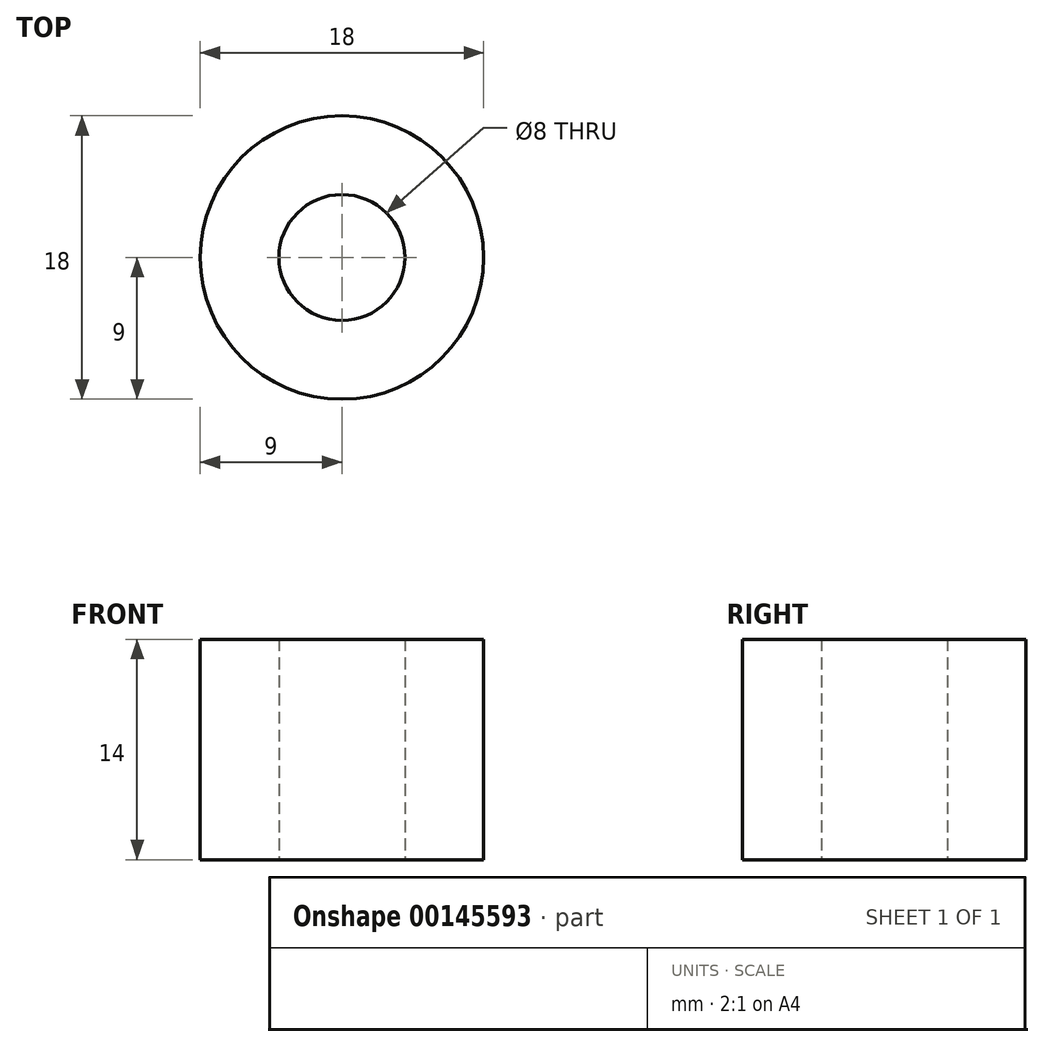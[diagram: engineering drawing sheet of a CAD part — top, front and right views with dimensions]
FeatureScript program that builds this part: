
annotation { "Feature Type Name" : "Feature", "Feature Type Description" : "" }
export const myFeature = defineFeature(function(context is Context, id is Id, definition is map)
    precondition{}
    {
        {
            var Q0;
            Q0=qCreatedBy(makeId("Top.planeOp"),FACE);
            var sketch = newSketch(context, id + "F0", { "sketchPlane" : qUnion([Q0])});
            skLineSegment(sketch, "E0.bottom", {"start": v(0, 0) * mm, "end": v(52, 0) * mm});
            skLineSegment(sketch, "E0.top", {"start": v(0, 22) * mm, "end": v(52, 22) * mm});
            skLineSegment(sketch, "E0.left", {"start": v(0, 0) * mm, "end": v(0, 22) * mm});
            skLineSegment(sketch, "E0.right", {"start": v(52, 0) * mm, "end": v(52, 22) * mm});
            skCircle(sketch, "E1", {"center": v(52, -18) * mm, "radius": 4 * mm});
            skCircle(sketch, "E2", {"center": v(52, -18) * mm, "radius": 9 * mm});
            skLineSegment(sketch, "E3.bottom", {"start": v(52, 0) * mm, "end": v(47, 0) * mm});
            skLineSegment(sketch, "E3.right", {"start": v(47, 0) * mm, "end": v(47, -10.52) * mm});
            skPoint(sketch, "E4", {"position": v(52, 11) * mm});
            skPoint(sketch, "E5", {"position": v(0, 11) * mm});
            skLineSegment(sketch, "E6", {"start": v(0, 11) * mm, "end": v(52, 11) * mm, "construction": true});
            skLineSegment(sketch, "E7", {"start": v(52, 0) * mm, "end": v(52, -18) * mm});
            skSolve(sketch);
        }
        {
            var Q0;
            {var subQ1=sQuery(id+"F0.wireOp",EDGE,"E0.top");Q0=makeQuery(id+"F0.imprint","IMPRINT",FACE,{"disambiguationData":[TD([[makeQuery(id+"F0.imprint","IMPRINT",EDGE,{"derivedFrom":subQ1}),-1.0]])]});}
            var Q1;
            {var subQ5=sQuery(id+"F0.wireOp",EDGE,"E2");var subQ6=sQuery(id+"F0.wireOp",EDGE,"E0.bottom");var subQ7=makeQuery(id+"F0.imprint","INTERSECT",VERTEX,{"derivedFrom":[subQ6,subQ5]});Q1=makeQuery(id+"F0.imprint","IMPRINT",FACE,{"disambiguationData":[TD([[makeQuery(id+"F0.imprint","IMPRINT",EDGE,{"disambiguationData":[TD([[subQ7,1.0]])],"derivedFrom":subQ6}),1.0]])]});}
            extrude(context, id + "F1", {"entities" : qUnion([Q0, Q1]), "depth" : 52.6 * mm});
        }
        {
            var Q0;
            {var subQ5=sQuery(id+"F0.wireOp",EDGE,"E3.bottom");Q0=makeQuery(id+"F0.imprint","IMPRINT",FACE,{"disambiguationData":[TD([[makeQuery(id+"F0.imprint","IMPRINT",EDGE,{"derivedFrom":subQ5}),1.0]])]});}
            var Q1;
            {var subQ2=sQuery(id+"F0.wireOp",EDGE,"E2");var subQ7=makeQuery(id+"F0.imprint","INTERSECT",VERTEX,{"derivedFrom":[subQ2,sQuery(id+"F0.wireOp",EDGE,"E3.right")]});Q1=makeQuery(id+"F0.imprint","IMPRINT",FACE,{"disambiguationData":[TD([[makeQuery(id+"F0.imprint","IMPRINT",EDGE,{"disambiguationData":[TD([[subQ7,1.0]])],"derivedFrom":subQ2}),1.0]])]});}
            var Q2;
            {var subQ1=sQuery(id+"F0.wireOp",EDGE,"E1");Q2=makeQuery(id+"F0.imprint","IMPRINT",FACE,{"disambiguationData":[TD([[makeQuery(id+"F0.imprint","IMPRINT",EDGE,{"derivedFrom":subQ1}),-1.0]])]});}
            extrude(context, id + "F2", {"entities" : qUnion([Q0, Q1, Q2]), "operationType" : NewBodyOperationType.ADD, "depth" : 14 * mm, "offsetDistance" : 25 * mm});
        }
        {
            var Q0;
            Q0=makeQuery(id+"F1.opExtrude","SWEPT_FACE",FACE,{"disambiguationData":[OSD([sQuery(id+"F0.wireOp",EDGE,"E0.left")])]});
            var sketch = newSketch(context, id + "F3", { "sketchPlane" : qUnion([Q0])});
            skCircle(sketch, "E8", {"center": v(-11, 9) * mm, "radius": 7.5 * mm});
            skLineSegment(sketch, "E9", {"start": v(-22, 47.6) * mm, "end": v(0, 47.6) * mm, "construction": true});
            skLineSegment(sketch, "E10", {"start": v(-22, 9) * mm, "end": v(0, 9) * mm, "construction": true});
            skLineSegment(sketch, "E11", {"start": v(-11, 9) * mm, "end": v(-11, 0) * mm, "construction": true});
            skLineSegment(sketch, "E12", {"start": v(-11, 0) * mm, "end": v(-11.5, 0) * mm});
            skLineSegment(sketch, "E13", {"start": v(-11.5, 0) * mm, "end": v(-11.5, 1.52) * mm});
            skLineSegment(sketch, "E14", {"start": v(-11.5, 1.52) * mm, "end": v(-10.5, 1.52) * mm});
            skLineSegment(sketch, "E15", {"start": v(-10.5, 1.52) * mm, "end": v(-10.5, 0) * mm});
            skLineSegment(sketch, "E16", {"start": v(-10.5, 0) * mm, "end": v(-11, 0) * mm});
            skCircle(sketch, "E17", {"center": v(-11, 47.6) * mm, "radius": 7.45 * mm});
            skLineSegment(sketch, "E18", {"start": v(-11, 47.6) * mm, "end": v(-11, 9) * mm, "construction": true});
            skLineSegment(sketch, "E19", {"start": v(-11, 19.6) * mm, "end": v(-16.3, 14.3) * mm, "construction": true});
            skLineSegment(sketch, "E20", {"start": v(-16.3, 14.3) * mm, "end": v(-11, 19.6) * mm});
            skLineSegment(sketch, "E21", {"start": v(-5.7, 14.3) * mm, "end": v(-11, 19.6) * mm});
            skLineSegment(sketch, "E22", {"start": v(-18.41, 17) * mm, "end": v(-3.44, 17) * mm});
            skSolve(sketch);
        }
        {
            var Q0;
            {var subQ0=sQuery(id+"F3.wireOp",EDGE,"E14");Q0=makeQuery(id+"F3.imprint","IMPRINT",FACE,{"disambiguationData":[TD([[makeQuery(id+"F3.imprint","IMPRINT",EDGE,{"derivedFrom":subQ0}),1.0]])]});}
            var Q1;
            {var subQ0=sQuery(id+"F3.wireOp",EDGE,"E20");var subQ1=sQuery(id+"F3.wireOp",EDGE,"E8");var subQ2=makeQuery(id+"F3.imprint","INTERSECT",VERTEX,{"derivedFrom":[subQ1,subQ0]});Q1=makeQuery(id+"F3.imprint","IMPRINT",FACE,{"disambiguationData":[TD([[makeQuery(id+"F3.imprint","IMPRINT",EDGE,{"disambiguationData":[TD([[subQ2,1.0]])],"derivedFrom":subQ1}),-1.0]])]});}
            var Q2;
            {var subQ0=sQuery(id+"F3.wireOp",EDGE,"E21");var subQ1=sQuery(id+"F3.wireOp",EDGE,"E8");var subQ2=makeQuery(id+"F3.imprint","INTERSECT",VERTEX,{"derivedFrom":[subQ1,subQ0]});Q2=makeQuery(id+"F3.imprint","IMPRINT",FACE,{"disambiguationData":[TD([[makeQuery(id+"F3.imprint","IMPRINT",EDGE,{"disambiguationData":[TD([[subQ2,-1.0]])],"derivedFrom":subQ1}),-1.0]])]});}
            var Q3;
            {var subQ0=sQuery(id+"F3.wireOp",EDGE,"035e7980-5c30-4cae-b493-835d1dc4b1b4");var subQ1=makeQuery(id+"F1.opExtrude","CAP_EDGE",EDGE,{"disambiguationData":[OSD([sQuery(id+"F0.wireOp",EDGE,"E0.left")])],"isStart":false});var subQ2=makeQuery(id+"F3.imprint","INTERSECT",VERTEX,{"disambiguationData":[OD(0.0)],"derivedFrom":[subQ1,subQ0]});Q3=makeQuery(id+"F3.imprint","IMPRINT",FACE,{"disambiguationData":[TD([[makeQuery(id+"F3.imprint","IMPRINT",EDGE,{"disambiguationData":[TD([[subQ2,1.0]])],"derivedFrom":subQ0}),-1.0]])]});}
            var Q4;
            {var subQ0=sQuery(id+"F3.wireOp",EDGE,"035e7980-5c30-4cae-b493-835d1dc4b1b4");var subQ1=makeQuery(id+"F1.opExtrude","CAP_EDGE",EDGE,{"disambiguationData":[OSD([sQuery(id+"F0.wireOp",EDGE,"E0.left")])],"isStart":false});var subQ2=makeQuery(id+"F3.imprint","INTERSECT",VERTEX,{"disambiguationData":[OD(0.0)],"derivedFrom":[subQ1,subQ0]});Q4=makeQuery(id+"F3.imprint","IMPRINT",FACE,{"disambiguationData":[TD([[makeQuery(id+"F3.imprint","IMPRINT",EDGE,{"disambiguationData":[TD([[subQ2,1.0]])],"derivedFrom":subQ0}),1.0]])]});}
            var Q5;
            Q5=makeQuery(id+"F3.imprint","IMPRINT",FACE,{"disambiguationData":[TD([[makeQuery(id+"F3.imprint","IMPRINT",EDGE,{"derivedFrom":sQuery(id+"F3.wireOp",EDGE,"E12")}),-1.0]])]});
            var Q6;
            {var subQ0=sQuery(id+"F3.wireOp",EDGE,"E17");var subQ1=makeQuery(id+"F1.opExtrude","CAP_EDGE",EDGE,{"disambiguationData":[OSD([sQuery(id+"F0.wireOp",EDGE,"E0.left")])],"isStart":false});var subQ2=makeQuery(id+"F3.imprint","INTERSECT",VERTEX,{"disambiguationData":[OD(0.0)],"derivedFrom":[subQ1,subQ0]});Q6=makeQuery(id+"F3.imprint","IMPRINT",FACE,{"disambiguationData":[TD([[makeQuery(id+"F3.imprint","IMPRINT",EDGE,{"disambiguationData":[TD([[subQ2,1.0]])],"derivedFrom":subQ0}),1.0]])]});}
            extrude(context, id + "F4", {"entities" : qUnion([Q0, Q1, Q2, Q3, Q4, Q5, Q6]), "operationType" : NewBodyOperationType.REMOVE, "endBound" : BoundingType.THROUGH_ALL, "oppositeDirection" : true, "depth" : 25 * mm, "offsetDistance" : 25 * mm});
        }
        {
            var Q0;
            Q0=makeQuery(id+"F1.opExtrude","SWEPT_FACE",FACE,{"disambiguationData":[OSD([sQuery(id+"F0.wireOp",EDGE,"E0.bottom")])]});
            var sketch = newSketch(context, id + "F5", { "sketchPlane" : qUnion([Q0])});
            skLineSegment(sketch, "E23.bottom", {"start": v(0, 29.9) * mm, "end": v(10, 29.9) * mm});
            skLineSegment(sketch, "E23.top", {"start": v(0, 9.9) * mm, "end": v(10, 9.9) * mm});
            skLineSegment(sketch, "E23.left", {"start": v(0, 29.9) * mm, "end": v(0, 9.9) * mm});
            skLineSegment(sketch, "E23.right", {"start": v(10, 29.9) * mm, "end": v(10, 9.9) * mm});
            skLineSegment(sketch, "E24.bottom", {"start": v(52, 41.1) * mm, "end": v(42, 41.1) * mm});
            skLineSegment(sketch, "E24.top", {"start": v(52, 21.1) * mm, "end": v(42, 21.1) * mm});
            skLineSegment(sketch, "E24.left", {"start": v(52, 41.1) * mm, "end": v(52, 21.1) * mm});
            skLineSegment(sketch, "E24.right", {"start": v(42, 41.1) * mm, "end": v(42, 21.1) * mm});
            skPoint(sketch, "E25", {"position": v(0, 9.4) * mm});
            skPoint(sketch, "E26", {"position": v(26, 52.6) * mm});
            skLineSegment(sketch, "E27", {"start": v(26, 52.6) * mm, "end": v(26, 0) * mm, "construction": true});
            skLineSegment(sketch, "E28.bottom", {"start": v(21, 52.6) * mm, "end": v(31, 52.6) * mm});
            skLineSegment(sketch, "E28.top", {"start": v(21, 37.6) * mm, "end": v(31, 37.6) * mm});
            skLineSegment(sketch, "E28.left", {"start": v(21, 52.6) * mm, "end": v(21, 37.6) * mm});
            skLineSegment(sketch, "E28.right", {"start": v(31, 52.6) * mm, "end": v(31, 37.6) * mm});
            skLineSegment(sketch, "E29", {"start": v(7, 52.6) * mm, "end": v(7, 29.9) * mm, "construction": true});
            skCircle(sketch, "E30", {"center": v(7, 44.9) * mm, "radius": 0.8 * mm});
            skCircle(sketch, "E31", {"center": v(7, 34.9) * mm, "radius": 0.8 * mm});
            skSolve(sketch);
        }
        {
            var Q0;
            Q0=makeQuery(id+"F5.imprint","IMPRINT",FACE,{"disambiguationData":[TD([[makeQuery(id+"F5.imprint","IMPRINT",EDGE,{"derivedFrom":sQuery(id+"F5.wireOp",EDGE,"E31")}),1.0]])]});
            extrude(context, id + "F6", {"entities" : qUnion([Q0]), "operationType" : NewBodyOperationType.REMOVE, "oppositeDirection" : true, "depth" : 7 * mm, "offsetDistance" : 25 * mm});
        }
        {
            var Q0;
            Q0=makeQuery(id+"F5.imprint","IMPRINT",FACE,{"disambiguationData":[TD([[makeQuery(id+"F5.imprint","IMPRINT",EDGE,{"derivedFrom":sQuery(id+"F5.wireOp",EDGE,"E30")}),1.0]])]});
            var Q1;
            Q1=sQuery(id+"F5.wireOp",EDGE,"E30");
            extrude(context, id + "F7", {"entities" : qUnion([Q0]), "operationType" : NewBodyOperationType.REMOVE, "surfaceEntities" : qUnion([Q1]), "oppositeDirection" : true, "depth" : 3 * mm, "offsetDistance" : 25 * mm});
        }
        {
            var Q0;
            Q0=makeQuery(id+"F5.imprint","IMPRINT",FACE,{"disambiguationData":[TD([[makeQuery(id+"F5.imprint","IMPRINT",EDGE,{"derivedFrom":sQuery(id+"F5.wireOp",EDGE,"E23.bottom")}),-1.0]])]});
            var Q1;
            Q1=makeQuery(id+"F5.imprint","IMPRINT",FACE,{"disambiguationData":[TD([[makeQuery(id+"F5.imprint","IMPRINT",EDGE,{"derivedFrom":sQuery(id+"F5.wireOp",EDGE,"E24.bottom")}),1.0]])]});
            extrude(context, id + "F8", {"entities" : qUnion([Q0, Q1]), "operationType" : NewBodyOperationType.ADD, "depth" : 7 * mm, "offsetDistance" : 25 * mm});
        }
        {
            var Q0;
            Q0=makeQuery(id+"F8.opExtrude","CAP_EDGE",EDGE,{"disambiguationData":[OSD([sQuery(id+"F5.wireOp",EDGE,"E23.top")])],"isStart":false});
            var Q1;
            Q1=makeQuery(id+"F8.opExtrude","CAP_EDGE",EDGE,{"disambiguationData":[OSD([sQuery(id+"F5.wireOp",EDGE,"E24.top")])],"isStart":false});
            chamfer(context, id + "F9", {"entities" : qUnion([Q0, Q1]), "width" : 10 * mm, "tangentPropagation" : true});
        }
        {
            var Q0;
            Q0=makeQuery(id+"F8.opExtrude","SWEPT_FACE",FACE,{"disambiguationData":[OSD([sQuery(id+"F5.wireOp",EDGE,"E23.bottom")])]});
            var sketch = newSketch(context, id + "F10", { "sketchPlane" : qUnion([Q0])});
            skLineSegment(sketch, "E32", {"start": v(-935.9, 0) * mm, "end": v(-935.88, -4.54) * mm});
            skLineSegment(sketch, "E33.left", {"start": v(0, -3.25) * mm, "end": v(0, -1.6) * mm});
            skLineSegment(sketch, "E34", {"start": v(6, -2.5) * mm, "end": v(7, -2.5) * mm});
            skLineSegment(sketch, "E35", {"start": v(4, -2.5) * mm, "end": v(5, -2.5) * mm});
            skLineSegment(sketch, "E36", {"start": v(0, -2.5) * mm, "end": v(1, -2.5) * mm});
            skLineSegment(sketch, "E37", {"start": v(7, -1.6) * mm, "end": v(8, -1.6) * mm});
            skLineSegment(sketch, "E38", {"start": v(2, -2.5) * mm, "end": v(3, -2.5) * mm});
            skLineSegment(sketch, "E39", {"start": v(3, -1.6) * mm, "end": v(4, -1.6) * mm});
            skLineSegment(sketch, "E40", {"start": v(8, -2.5) * mm, "end": v(9, -2.5) * mm});
            skLineSegment(sketch, "E41", {"start": v(8, -1.6) * mm, "end": v(8, -2.5) * mm});
            skLineSegment(sketch, "E42", {"start": v(9, -2.5) * mm, "end": v(9, -1.6) * mm});
            skLineSegment(sketch, "E43", {"start": v(10, -1.6) * mm, "end": v(10, -2.5) * mm});
            skLineSegment(sketch, "E44", {"start": v(6, -1.6) * mm, "end": v(6, -2.5) * mm});
            skLineSegment(sketch, "E45", {"start": v(2, -1.6) * mm, "end": v(2, -2.5) * mm});
            skLineSegment(sketch, "E46", {"start": v(1, -1.6) * mm, "end": v(2, -1.6) * mm});
            skLineSegment(sketch, "E47", {"start": v(1, -2.5) * mm, "end": v(1, -1.6) * mm});
            skLineSegment(sketch, "E48", {"start": v(9, -1.6) * mm, "end": v(10, -1.6) * mm});
            skLineSegment(sketch, "E49", {"start": v(5, -1.6) * mm, "end": v(6, -1.6) * mm});
            skLineSegment(sketch, "E50", {"start": v(5, -2.5) * mm, "end": v(5, -1.6) * mm});
            skLineSegment(sketch, "E51", {"start": v(3, -2.5) * mm, "end": v(3, -1.6) * mm});
            skLineSegment(sketch, "E52", {"start": v(4, -1.6) * mm, "end": v(4, -2.5) * mm});
            skLineSegment(sketch, "E53", {"start": v(7, -2.5) * mm, "end": v(7, -1.6) * mm});
            skLineSegment(sketch, "E54", {"start": v(0, -1.6) * mm, "end": v(0, -2.5) * mm});
            skLineSegment(sketch, "E55", {"start": v(10, -2.5) * mm, "end": v(10, -3.25) * mm});
            skLineSegment(sketch, "E56", {"start": v(0, -3.25) * mm, "end": v(10, -3.25) * mm});
            skLineSegment(sketch, "E57", {"start": v(5.3, -1.6) * mm, "end": v(5.3, 0) * mm});
            skSolve(sketch);
        }
        {
            var Q0;
            Q0=qSketchRegion(id+"F10",true);
            extrude(context, id + "F11", {"entities" : qUnion([Q0]), "operationType" : NewBodyOperationType.REMOVE, "oppositeDirection" : true, "depth" : 6 * mm});
        }
        {
            var Q0;
            Q0=makeQuery(id+"F8.opExtrude","SWEPT_FACE",FACE,{"disambiguationData":[OSD([sQuery(id+"F5.wireOp",EDGE,"E24.bottom")])]});
            var sketch = newSketch(context, id + "F12", { "sketchPlane" : qUnion([Q0])});
            skLineSegment(sketch, "E58.left", {"start": v(42, -3.25) * mm, "end": v(42, -1.6) * mm});
            skLineSegment(sketch, "E59", {"start": v(48, -2.5) * mm, "end": v(49, -2.5) * mm});
            skLineSegment(sketch, "E60", {"start": v(46, -2.5) * mm, "end": v(47, -2.5) * mm});
            skLineSegment(sketch, "E61", {"start": v(42, -2.5) * mm, "end": v(43, -2.5) * mm});
            skLineSegment(sketch, "E62", {"start": v(49, -1.6) * mm, "end": v(50, -1.6) * mm});
            skLineSegment(sketch, "E63", {"start": v(44, -2.5) * mm, "end": v(45, -2.5) * mm});
            skLineSegment(sketch, "E64", {"start": v(45, -1.6) * mm, "end": v(46, -1.6) * mm});
            skLineSegment(sketch, "E65", {"start": v(50, -2.5) * mm, "end": v(51, -2.5) * mm});
            skLineSegment(sketch, "E66", {"start": v(50, -1.6) * mm, "end": v(50, -2.5) * mm});
            skLineSegment(sketch, "E67", {"start": v(51, -2.5) * mm, "end": v(51, -1.6) * mm});
            skLineSegment(sketch, "E68", {"start": v(52, -1.6) * mm, "end": v(52, -2.5) * mm});
            skLineSegment(sketch, "E69", {"start": v(48, -1.6) * mm, "end": v(48, -2.5) * mm});
            skLineSegment(sketch, "E70", {"start": v(44, -1.6) * mm, "end": v(44, -2.5) * mm});
            skLineSegment(sketch, "E71", {"start": v(43, -1.6) * mm, "end": v(44, -1.6) * mm});
            skLineSegment(sketch, "E72", {"start": v(43, -2.5) * mm, "end": v(43, -1.6) * mm});
            skLineSegment(sketch, "E73", {"start": v(51, -1.6) * mm, "end": v(52, -1.6) * mm});
            skLineSegment(sketch, "E74", {"start": v(47, -1.6) * mm, "end": v(48, -1.6) * mm});
            skLineSegment(sketch, "E75", {"start": v(47, -2.5) * mm, "end": v(47, -1.6) * mm});
            skLineSegment(sketch, "E76", {"start": v(45, -2.5) * mm, "end": v(45, -1.6) * mm});
            skLineSegment(sketch, "E77", {"start": v(46, -1.6) * mm, "end": v(46, -2.5) * mm});
            skLineSegment(sketch, "E78", {"start": v(49, -2.5) * mm, "end": v(49, -1.6) * mm});
            skLineSegment(sketch, "E79", {"start": v(42, -1.6) * mm, "end": v(42, -2.5) * mm});
            skLineSegment(sketch, "E80", {"start": v(52, -2.5) * mm, "end": v(52, -3.25) * mm});
            skLineSegment(sketch, "E81", {"start": v(42, -3.25) * mm, "end": v(52, -3.25) * mm});
            skLineSegment(sketch, "E82", {"start": v(47.23, -1.6) * mm, "end": v(47.23, 0) * mm});
            skSolve(sketch);
        }
        {
            var Q0;
            Q0=qSketchRegion(id+"F12",true);
            extrude(context, id + "F13", {"entities" : qUnion([Q0]), "operationType" : NewBodyOperationType.REMOVE, "oppositeDirection" : true, "depth" : 6 * mm});
        }
        {
            var Q0;
            Q0=makeQuery(id+"F1.opExtrude","SWEPT_FACE",FACE,{"disambiguationData":[OSD([sQuery(id+"F0.wireOp",EDGE,"E0.top")])]});
            var sketch = newSketch(context, id + "F14", { "sketchPlane" : qUnion([Q0])});
            skLineSegment(sketch, "E83.bottom", {"start": v(-52, 9.9) * mm, "end": v(-42, 9.9) * mm});
            skLineSegment(sketch, "E83.top", {"start": v(-52, 29.9) * mm, "end": v(-42, 29.9) * mm});
            skLineSegment(sketch, "E83.left", {"start": v(-52, 9.9) * mm, "end": v(-52, 29.9) * mm});
            skLineSegment(sketch, "E83.right", {"start": v(-42, 9.9) * mm, "end": v(-42, 29.9) * mm});
            skLineSegment(sketch, "E84.bottom", {"start": v(0, 41.1) * mm, "end": v(-10, 41.1) * mm});
            skLineSegment(sketch, "E84.top", {"start": v(0, 21.1) * mm, "end": v(-10, 21.1) * mm});
            skLineSegment(sketch, "E84.left", {"start": v(0, 41.1) * mm, "end": v(0, 21.1) * mm});
            skLineSegment(sketch, "E84.right", {"start": v(-10, 41.1) * mm, "end": v(-10, 21.1) * mm});
            skSolve(sketch);
        }
        {
            var Q0;
            Q0=qSketchRegion(id+"F14",true);
            extrude(context, id + "F15", {"entities" : qUnion([Q0]), "operationType" : NewBodyOperationType.ADD, "depth" : 7 * mm});
        }
        {
            var Q0;
            Q0=makeQuery(id+"F15.opExtrude","CAP_EDGE",EDGE,{"disambiguationData":[OSD([sQuery(id+"F14.wireOp",EDGE,"E84.top")])],"isStart":false});
            var Q1;
            Q1=makeQuery(id+"F15.opExtrude","CAP_EDGE",EDGE,{"disambiguationData":[OSD([sQuery(id+"F14.wireOp",EDGE,"E83.bottom")])],"isStart":false});
            chamfer(context, id + "F16", {"entities" : qUnion([Q0, Q1]), "width" : 10 * mm, "tangentPropagation" : true});
        }
        {
            var Q0;
            Q0=makeQuery(id+"F15.opExtrude","SWEPT_FACE",FACE,{"disambiguationData":[OSD([sQuery(id+"F14.wireOp",EDGE,"E83.top")])]});
            var sketch = newSketch(context, id + "F17", { "sketchPlane" : qUnion([Q0])});
            skLineSegment(sketch, "E85.left", {"start": v(42, 23.6) * mm, "end": v(42, 25.25) * mm});
            skLineSegment(sketch, "E86", {"start": v(48, 24.35) * mm, "end": v(49, 24.35) * mm});
            skLineSegment(sketch, "E87", {"start": v(46, 24.35) * mm, "end": v(47, 24.35) * mm});
            skLineSegment(sketch, "E88", {"start": v(42, 24.35) * mm, "end": v(43, 24.35) * mm});
            skLineSegment(sketch, "E89", {"start": v(49, 25.25) * mm, "end": v(50, 25.25) * mm});
            skLineSegment(sketch, "E90", {"start": v(44, 24.35) * mm, "end": v(45, 24.35) * mm});
            skLineSegment(sketch, "E91", {"start": v(45, 25.25) * mm, "end": v(46, 25.25) * mm});
            skLineSegment(sketch, "E92", {"start": v(50, 24.35) * mm, "end": v(51, 24.35) * mm});
            skLineSegment(sketch, "E93", {"start": v(50, 25.25) * mm, "end": v(50, 24.35) * mm});
            skLineSegment(sketch, "E94", {"start": v(51, 24.35) * mm, "end": v(51, 25.25) * mm});
            skLineSegment(sketch, "E95", {"start": v(52, 25.25) * mm, "end": v(52, 24.35) * mm});
            skLineSegment(sketch, "E96", {"start": v(48, 25.25) * mm, "end": v(48, 24.35) * mm});
            skLineSegment(sketch, "E97", {"start": v(44, 25.25) * mm, "end": v(44, 24.35) * mm});
            skLineSegment(sketch, "E98", {"start": v(43, 25.25) * mm, "end": v(44, 25.25) * mm});
            skLineSegment(sketch, "E99", {"start": v(43, 24.35) * mm, "end": v(43, 25.25) * mm});
            skLineSegment(sketch, "E100", {"start": v(51, 25.25) * mm, "end": v(52, 25.25) * mm});
            skLineSegment(sketch, "E101", {"start": v(47, 25.25) * mm, "end": v(48, 25.25) * mm});
            skLineSegment(sketch, "E102", {"start": v(47, 24.35) * mm, "end": v(47, 25.25) * mm});
            skLineSegment(sketch, "E103", {"start": v(45, 24.35) * mm, "end": v(45, 25.25) * mm});
            skLineSegment(sketch, "E104", {"start": v(46, 25.25) * mm, "end": v(46, 24.35) * mm});
            skLineSegment(sketch, "E105", {"start": v(49, 24.35) * mm, "end": v(49, 25.25) * mm});
            skLineSegment(sketch, "E106", {"start": v(42, 25.25) * mm, "end": v(42, 24.35) * mm});
            skLineSegment(sketch, "E107", {"start": v(52, 24.35) * mm, "end": v(52, 23.6) * mm});
            skLineSegment(sketch, "E108", {"start": v(42, 23.6) * mm, "end": v(52, 23.6) * mm});
            skLineSegment(sketch, "E109", {"start": v(47, 23.6) * mm, "end": v(47, 22) * mm});
            skSolve(sketch);
        }
        {
            var Q0;
            {var subQ4=sQuery(id+"F17.wireOp",EDGE,"E85.left");Q0=makeQuery(id+"F17.imprint","IMPRINT",FACE,{"disambiguationData":[TD([[makeQuery(id+"F17.imprint","IMPRINT",EDGE,{"derivedFrom":subQ4}),1.0]])]});}
            extrude(context, id + "F18", {"entities" : qUnion([Q0]), "operationType" : NewBodyOperationType.REMOVE, "oppositeDirection" : true, "depth" : 6 * mm});
        }
        {
            var Q0;
            Q0=makeQuery(id+"F15.opExtrude","SWEPT_FACE",FACE,{"disambiguationData":[OSD([sQuery(id+"F14.wireOp",EDGE,"E84.bottom")])]});
            var sketch = newSketch(context, id + "F19", { "sketchPlane" : qUnion([Q0])});
            skLineSegment(sketch, "E110", {"start": v(6, 24.35) * mm, "end": v(7, 24.35) * mm});
            skLineSegment(sketch, "E111", {"start": v(4, 24.35) * mm, "end": v(5, 24.35) * mm});
            skLineSegment(sketch, "E112", {"start": v(0, 24.35) * mm, "end": v(1, 24.35) * mm});
            skLineSegment(sketch, "E113", {"start": v(7, 25.25) * mm, "end": v(8, 25.25) * mm});
            skLineSegment(sketch, "E114", {"start": v(2, 24.35) * mm, "end": v(3, 24.35) * mm});
            skLineSegment(sketch, "E115", {"start": v(3, 25.25) * mm, "end": v(4, 25.25) * mm});
            skLineSegment(sketch, "E116", {"start": v(8, 24.35) * mm, "end": v(9, 24.35) * mm});
            skLineSegment(sketch, "E117", {"start": v(8, 25.25) * mm, "end": v(8, 24.35) * mm});
            skLineSegment(sketch, "E118", {"start": v(9, 24.35) * mm, "end": v(9, 25.25) * mm});
            skLineSegment(sketch, "E119", {"start": v(10, 25.25) * mm, "end": v(10, 24.35) * mm});
            skLineSegment(sketch, "E120", {"start": v(6, 25.25) * mm, "end": v(6, 24.35) * mm});
            skLineSegment(sketch, "E121", {"start": v(2, 25.25) * mm, "end": v(2, 24.35) * mm});
            skLineSegment(sketch, "E122", {"start": v(1, 25.25) * mm, "end": v(2, 25.25) * mm});
            skLineSegment(sketch, "E123", {"start": v(1, 24.35) * mm, "end": v(1, 25.25) * mm});
            skLineSegment(sketch, "E124", {"start": v(9, 25.25) * mm, "end": v(10, 25.25) * mm});
            skLineSegment(sketch, "E125", {"start": v(5, 25.25) * mm, "end": v(6, 25.25) * mm});
            skLineSegment(sketch, "E126", {"start": v(5, 24.35) * mm, "end": v(5, 25.25) * mm});
            skLineSegment(sketch, "E127", {"start": v(3, 24.35) * mm, "end": v(3, 25.25) * mm});
            skLineSegment(sketch, "E128", {"start": v(4, 25.25) * mm, "end": v(4, 24.35) * mm});
            skLineSegment(sketch, "E129", {"start": v(7, 24.35) * mm, "end": v(7, 25.25) * mm});
            skLineSegment(sketch, "E130", {"start": v(0, 23.6) * mm, "end": v(10, 23.6) * mm});
            skSolve(sketch);
        }
        {
            var Q0;
            Q0=makeQuery(id+"F19.imprint","IMPRINT",FACE,{"disambiguationData":[TD([[makeQuery(id+"F19.imprint","IMPRINT",EDGE,{"derivedFrom":sQuery(id+"F19.wireOp",EDGE,"E110")}),-1.0]])]});
            extrude(context, id + "F20", {"entities" : qUnion([Q0]), "operationType" : NewBodyOperationType.REMOVE, "oppositeDirection" : true, "depth" : 6 * mm});
        }
        {
            var Q0;
            Q0=makeQuery(id+"F1.opExtrude","SWEPT_FACE",FACE,{"disambiguationData":[OSD([sQuery(id+"F0.wireOp",EDGE,"E0.top")])]});
            var sketch = newSketch(context, id + "F21", { "sketchPlane" : qUnion([Q0])});
            skCircle(sketch, "E131", {"center": v(-26, 15) * mm, "radius": 1.3 * mm});
            skPoint(sketch, "E132", {"position": v(-26, 52.6) * mm});
            skLineSegment(sketch, "E133", {"start": v(-26, 52.6) * mm, "end": v(-26, 0) * mm, "construction": true});
            skCircle(sketch, "E134", {"center": v(-30.5, 20) * mm, "radius": 1.3 * mm});
            skCircle(sketch, "E135", {"center": v(-21.5, 20) * mm, "radius": 1.3 * mm});
            skLineSegment(sketch, "E136", {"start": v(-52, 20) * mm, "end": v(0, 20) * mm, "construction": true});
            skCircle(sketch, "E137", {"center": v(-26, 35) * mm, "radius": 1.3 * mm});
            skCircle(sketch, "E138", {"center": v(-30.5, 30) * mm, "radius": 1.3 * mm});
            skCircle(sketch, "E139", {"center": v(-21.5, 30) * mm, "radius": 1.3 * mm});
            skSolve(sketch);
        }
        {
            var Q0;
            Q0=makeQuery(id+"F21.imprint","IMPRINT",FACE,{"disambiguationData":[TD([[makeQuery(id+"F21.imprint","IMPRINT",EDGE,{"derivedFrom":sQuery(id+"F21.wireOp",EDGE,"E134")}),1.0]])]});
            var Q1;
            Q1=makeQuery(id+"F21.imprint","IMPRINT",FACE,{"disambiguationData":[TD([[makeQuery(id+"F21.imprint","IMPRINT",EDGE,{"derivedFrom":sQuery(id+"F21.wireOp",EDGE,"E135")}),1.0]])]});
            var Q2;
            Q2=makeQuery(id+"F21.imprint","IMPRINT",FACE,{"disambiguationData":[TD([[makeQuery(id+"F21.imprint","IMPRINT",EDGE,{"derivedFrom":sQuery(id+"F21.wireOp",EDGE,"E138")}),1.0]])]});
            var Q3;
            Q3=makeQuery(id+"F21.imprint","IMPRINT",FACE,{"disambiguationData":[TD([[makeQuery(id+"F21.imprint","IMPRINT",EDGE,{"derivedFrom":sQuery(id+"F21.wireOp",EDGE,"E139")}),1.0]])]});
            extrude(context, id + "F22", {"entities" : qUnion([Q0, Q1, Q2, Q3]), "operationType" : NewBodyOperationType.REMOVE, "endBound" : BoundingType.THROUGH_ALL, "oppositeDirection" : true, "depth" : 17 * mm, "offsetDistance" : 25 * mm});
        }
        {
            var Q0;
            Q0=makeQuery(id+"F21.imprint","IMPRINT",FACE,{"disambiguationData":[TD([[makeQuery(id+"F21.imprint","IMPRINT",EDGE,{"derivedFrom":sQuery(id+"F21.wireOp",EDGE,"E131")}),1.0]])]});
            var Q1;
            Q1=makeQuery(id+"F21.imprint","IMPRINT",FACE,{"disambiguationData":[TD([[makeQuery(id+"F21.imprint","IMPRINT",EDGE,{"derivedFrom":sQuery(id+"F21.wireOp",EDGE,"E137")}),1.0]])]});
            extrude(context, id + "F23", {"entities" : qUnion([Q0, Q1]), "operationType" : NewBodyOperationType.REMOVE, "oppositeDirection" : true, "depth" : 5 * mm, "offsetDistance" : 25 * mm});
        }
        {
            var Q0;
            Q0=makeQuery(id+"F4.boolean.opBoolean","SPLIT",BODY,{"disambiguationData":[OD(0.0)],"derivedFrom":makeQuery(id+"F1.opExtrude","SWEPT_BODY",BODY,{"disambiguationData":[OSD([sQuery(id+"F0.wireOp",EDGE,"E0.bottom"),sQuery(id+"F0.wireOp",EDGE,"E0.top"),sQuery(id+"F0.wireOp",EDGE,"E0.left"),sQuery(id+"F0.wireOp",EDGE,"E0.right"),sQuery(id+"F0.wireOp",EDGE,"E2")])]})});
            deleteBodies(context, id + "F24", {"entities" : qUnion([Q0])});
        }
    });
